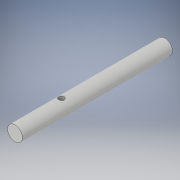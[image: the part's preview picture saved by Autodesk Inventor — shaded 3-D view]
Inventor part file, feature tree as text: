
AUTODESK INVENTOR PART (.ipt)
format: ipt  version: 2017 (Build 210142000, 142)  size: 99,840 bytes
history: native  units: in
note: dims shown in document units (in); Inventor stores cm internally (conversion verified against a paired STEP export)
features: extrude x2, sketch x2
ambient origin geometry x8: Origin, YZ Plane, XZ Plane, XY Plane, X Axis, Y Axis, Z Axis, Center Point
bodies: Solid1 (feature_tree)
feature tree (4):
  extrude  "Extrusion1"  Depth=3.189in TaperAngle=0.0deg
  extrude  "Extrusion2"  Depth=2.2047in TaperAngle=0.0deg
  sketch  "Sketch1"  dims[d0=0.315in d1=3.189in d2=0.0in]
  sketch  "Sketch2"  dims[d3=0.1181in d5=3.937in d6=0.0in d7=2.2047in]
